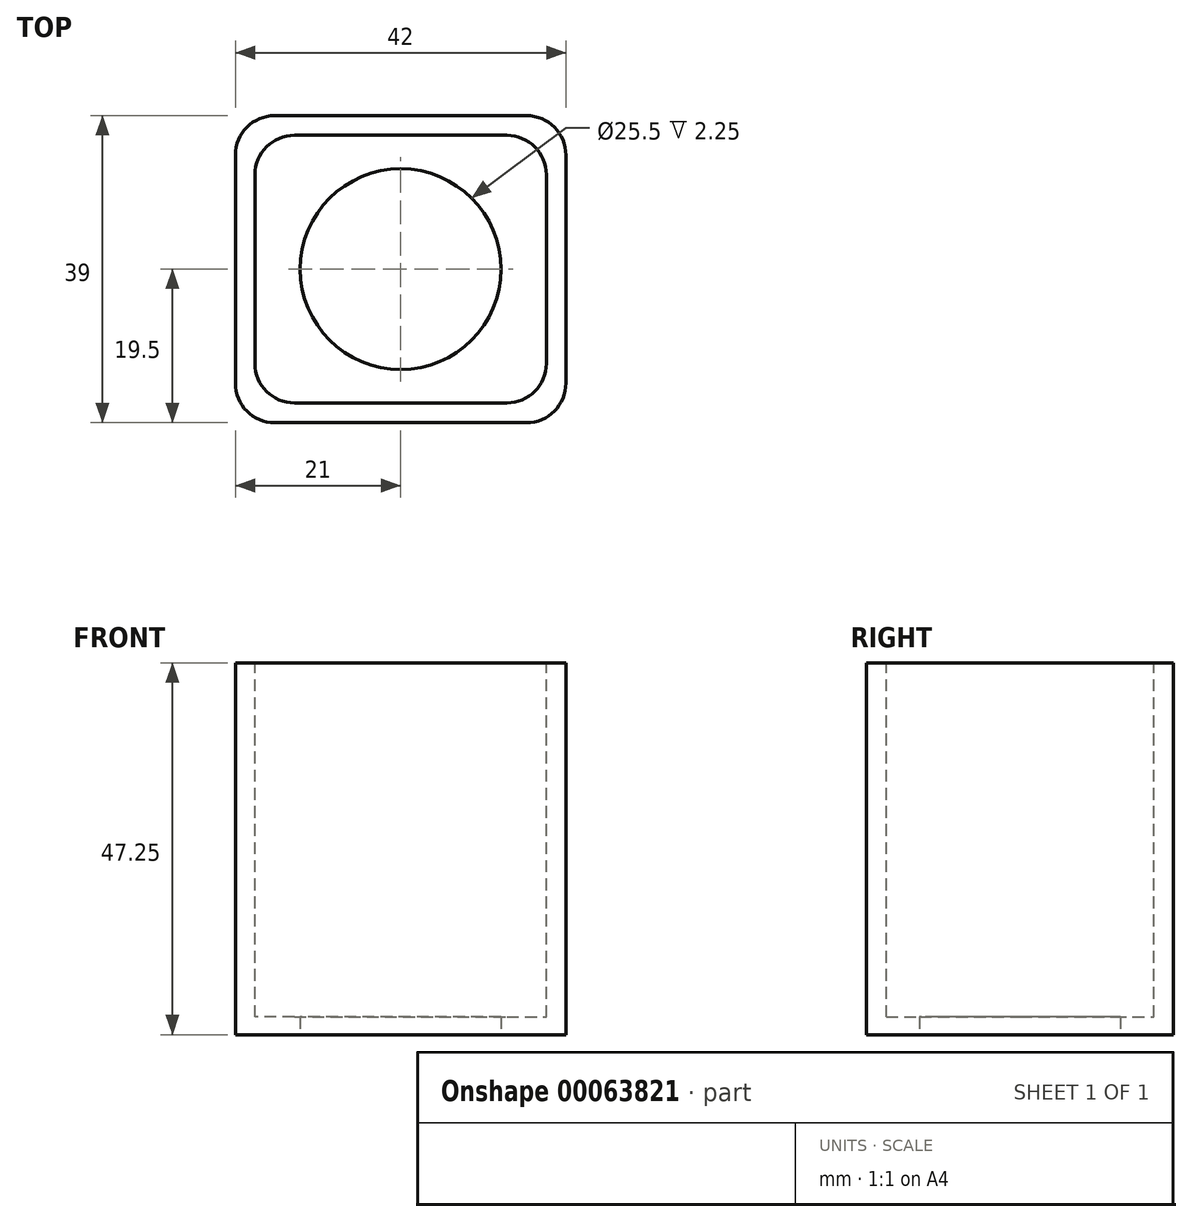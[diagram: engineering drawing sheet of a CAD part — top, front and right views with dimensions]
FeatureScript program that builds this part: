
annotation { "Feature Type Name" : "Feature", "Feature Type Description" : "" }
export const myFeature = defineFeature(function(context is Context, id is Id, definition is map)
    precondition{}
    {
        {
            var Q0;
            Q0=qCreatedBy(makeId("Top.planeOp"),FACE);
            var sketch = newSketch(context, id + "F0", { "sketchPlane" : qUnion([Q0])});
            skLineSegment(sketch, "E0.rect.bottom", {"start": v(-21, 19.5) * mm, "end": v(21, 19.5) * mm});
            skLineSegment(sketch, "E0.rect.top", {"start": v(-21, -19.5) * mm, "end": v(21, -19.5) * mm});
            skLineSegment(sketch, "E0.rect.left", {"start": v(-21, 19.5) * mm, "end": v(-21, -19.5) * mm});
            skLineSegment(sketch, "E0.rect.right", {"start": v(21, 19.5) * mm, "end": v(21, -19.5) * mm});
            skPoint(sketch, "E0.rect.middle", {"position": v(0, 0) * mm});
            skCircle(sketch, "E1", {"center": v(0, 0) * mm, "radius": 12.75 * mm});
            skSolve(sketch);
        }
        {
            var Q0;
            Q0=makeQuery(id+"F0.imprint","IMPRINT",FACE,{"disambiguationData":[TD([[makeQuery(id+"F0.imprint","IMPRINT",EDGE,{"derivedFrom":sQuery(id+"F0.wireOp",EDGE,"E0.rect.bottom")}),-1.0]])]});
            extrude(context, id + "F1", {"entities" : qUnion([Q0]), "depth" : 47.25 * mm});
        }
        {
            var Q0;
            Q0=makeQuery(id+"F1.opExtrude","CAP_FACE",FACE,{"disambiguationData":[OSD([sQuery(id+"F0.wireOp",EDGE,"E0.rect.bottom"),sQuery(id+"F0.wireOp",EDGE,"E0.rect.top"),sQuery(id+"F0.wireOp",EDGE,"E0.rect.left"),sQuery(id+"F0.wireOp",EDGE,"E0.rect.right"),sQuery(id+"F0.wireOp",EDGE,"E1")])],"isStart":false});
            var sketch = newSketch(context, id + "F2", { "sketchPlane" : qUnion([Q0])});
            skLineSegment(sketch, "E2.rect.bottom", {"start": v(-18.5, 17) * mm, "end": v(18.5, 17) * mm});
            skLineSegment(sketch, "E2.rect.top", {"start": v(-18.5, -17) * mm, "end": v(18.5, -17) * mm});
            skLineSegment(sketch, "E2.rect.left", {"start": v(-18.5, 17) * mm, "end": v(-18.5, -17) * mm});
            skLineSegment(sketch, "E2.rect.right", {"start": v(18.5, 17) * mm, "end": v(18.5, -17) * mm});
            skPoint(sketch, "E2.rect.middle", {"position": v(0, 0) * mm});
            skSolve(sketch);
        }
        {
            var Q0;
            Q0=makeQuery(id+"F2.imprint","IMPRINT",FACE,{"disambiguationData":[TD([[makeQuery(id+"F2.imprint","IMPRINT",EDGE,{"derivedFrom":sQuery(id+"F2.wireOp",EDGE,"E2.rect.bottom")}),-1.0]])]});
            extrude(context, id + "F3", {"entities" : qUnion([Q0]), "operationType" : NewBodyOperationType.REMOVE, "oppositeDirection" : true, "depth" : 45 * mm});
        }
        {
            var Q0;
            Q0=makeQuery(id+"F1.opExtrude","SWEPT_EDGE",EDGE,{"disambiguationData":[OSD([sQuery(id+"F0.wireOp",EDGE,"E0.rect.top"),sQuery(id+"F0.wireOp",EDGE,"E0.rect.left")])]});
            var Q1;
            Q1=makeQuery(id+"F1.opExtrude","SWEPT_EDGE",EDGE,{"disambiguationData":[OSD([sQuery(id+"F0.wireOp",EDGE,"E0.rect.top"),sQuery(id+"F0.wireOp",EDGE,"E0.rect.right")])]});
            var Q2;
            Q2=makeQuery(id+"F1.opExtrude","SWEPT_EDGE",EDGE,{"disambiguationData":[OSD([sQuery(id+"F0.wireOp",EDGE,"E0.rect.bottom"),sQuery(id+"F0.wireOp",EDGE,"E0.rect.right")])]});
            var Q3;
            Q3=makeQuery(id+"F1.opExtrude","SWEPT_EDGE",EDGE,{"disambiguationData":[OSD([sQuery(id+"F0.wireOp",EDGE,"E0.rect.bottom"),sQuery(id+"F0.wireOp",EDGE,"E0.rect.left")])]});
            var Q4;
            Q4=makeQuery(id+"F3.boolean.opBoolean","COPY",EDGE,{"derivedFrom":makeQuery(id+"F3.opExtrude","SWEPT_EDGE",EDGE,{"disambiguationData":[OSD([sQuery(id+"F2.wireOp",EDGE,"E2.rect.top"),sQuery(id+"F2.wireOp",EDGE,"E2.rect.left")])]})});
            var Q5;
            Q5=makeQuery(id+"F3.boolean.opBoolean","COPY",EDGE,{"derivedFrom":makeQuery(id+"F3.opExtrude","SWEPT_EDGE",EDGE,{"disambiguationData":[OSD([sQuery(id+"F2.wireOp",EDGE,"E2.rect.bottom"),sQuery(id+"F2.wireOp",EDGE,"E2.rect.left")])]})});
            var Q6;
            Q6=makeQuery(id+"F3.boolean.opBoolean","COPY",EDGE,{"derivedFrom":makeQuery(id+"F3.opExtrude","SWEPT_EDGE",EDGE,{"disambiguationData":[OSD([sQuery(id+"F2.wireOp",EDGE,"E2.rect.bottom"),sQuery(id+"F2.wireOp",EDGE,"E2.rect.right")])]})});
            var Q7;
            Q7=makeQuery(id+"F3.boolean.opBoolean","COPY",EDGE,{"derivedFrom":makeQuery(id+"F3.opExtrude","SWEPT_EDGE",EDGE,{"disambiguationData":[OSD([sQuery(id+"F2.wireOp",EDGE,"E2.rect.top"),sQuery(id+"F2.wireOp",EDGE,"E2.rect.right")])]})});
            fillet(context, id + "F4", {"entities" : qUnion([Q0, Q1, Q2, Q3, Q4, Q5, Q6, Q7]), "radius" : 5 * mm, "tangentPropagation" : true, "allowEdgeOverflow" : false});
        }
    });
